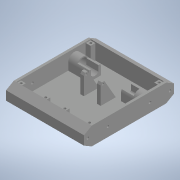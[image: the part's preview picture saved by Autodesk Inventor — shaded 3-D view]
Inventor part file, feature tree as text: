
AUTODESK INVENTOR PART (.ipt)
format: ipt  version: 2020 (Build 240168000, 168)  size: 398,336 bytes
history: native  units: in
note: dims shown in document units (in); Inventor stores cm internally (conversion verified against a paired STEP export)
features: projected_geometry x13, extrude x11, sketch x11, mirror x4, plane x1
ambient origin geometry x8: Origin, YZ Plane, XZ Plane, XY Plane, X Axis, Y Axis, Z Axis, Center Point
bodies: Solid1 (feature_tree)
feature tree (40):
  extrude  "Extrusion1"  Depth=5.9055in
  extrude  "Extrusion2"  TaperAngle=0.0deg  [1 undecoded]
  extrude  "Extrusion3"  Depth=1.063in
  extrude  "Extrusion4"  Depth=0.315in
  extrude  "Extrusion5"  TaperAngle=0.0deg  [1 undecoded]
  extrude  "Extrusion6"  Depth=0.5906in
  mirror  "Mirror1"
  extrude  "Extrusion7"  Depth=0.0787in
  mirror  "Mirror2"
  extrude  "Extrusion8"  Depth=0.5512in
  mirror  "Mirror3"
  plane  "Work Plane1"
  extrude  "Extrusion9"  Depth=0.7874in TaperAngle=0.0deg
  mirror  "Mirror4"
  extrude  "Extrusion10"  Depth=6.063in TaperAngle=0.0deg
  extrude  "Extrusion11"  Depth=0.1575in
  sketch  "Sketch1"  dims[d0=1.1811in d1=5.9055in]
  sketch  "Sketch2"  dims[d2=5.1181in d3=0.0in]
  projected_geometry  "Projected Loop1"
  sketch  "Sketch3"  dims[d4=0.1575in d5=1.063in]
  projected_geometry  "Projected Loop2"
  projected_geometry  "Projected Loop3"
  sketch  "Sketch4"  dims[d6=0.0in d8=0.315in]
  sketch  "Sketch5"  dims[d10=0.993in d11=0.0in]
  projected_geometry  "Projected Loop4"
  sketch  "Sketch6"  dims[d12=0.6496in d13=0.5906in]
  sketch  "Sketch7"  dims[d14=1.5748in d15=0.0787in]
  sketch  "Sketch9"  dims[d16=0.5512in d17=0.0in d18=0.6102in]
  sketch  "Sketch10"  dims[d19=0.4803in d20=0.7874in d21=0.0in]
  sketch  "Sketch12"  dims[d22=0.1654in d23=6.063in d24=0.0in]
  projected_geometry  "Projected Loop6"
  projected_geometry  "Projected Loop7"
  projected_geometry  "Projected Loop8"
  sketch  "Sketch13"  dims[d25=0.5114in d26=0.1575in d27=1.5748in d28=0.0in d29=0.0in d30=0.1575in d31=0.2756in d32=0.0in d33=0.4331in d34=0.122in d38=2.7559in d40=0.061in d41=0.0909in d42=0.2362in d43=0.0in d44=60.0deg d45=0.0787in d46=0.315in d48=0.993in d49=0.0in d51=0.1575in d52=0.1575in d53=0.2756in d54=0.0in d55=0.4724in]
  projected_geometry  "Projected Loop9"
  projected_geometry  "Projected Loop10"
  projected_geometry  "Projected Loop11"
  projected_geometry  "Projected Loop12"
  projected_geometry  "Projected Loop13"
  projected_geometry  "Projected Loop14"
note: 2 required parameter values undecoded (feature->parameter linkage not recoverable at this tier; creation-order binding heuristic only, values carry confidence <= 0.55)
